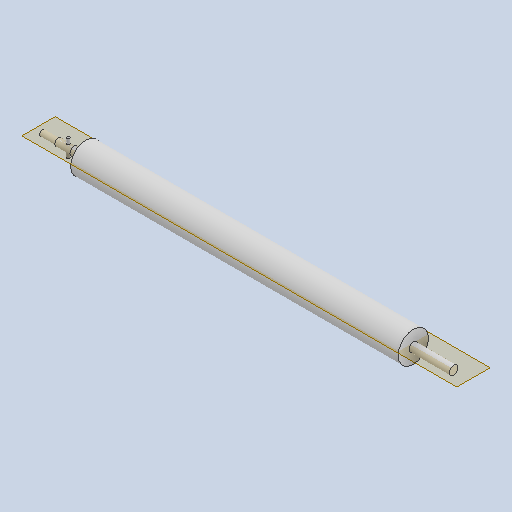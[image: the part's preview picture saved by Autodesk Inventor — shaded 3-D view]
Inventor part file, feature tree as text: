
AUTODESK INVENTOR PART (.ipt)
format: ipt  version: 2023 (Build 270158000, 158)  size: 115,712 bytes
history: native  units: in
note: dims shown in document units (in); Inventor stores cm internally (conversion verified against a paired STEP export)
features: extrude x6, sketch x6, plane x1
ambient origin geometry x8: Origin, YZ Plane, XZ Plane, XY Plane, X Axis, Y Axis, Z Axis, Center Point
bodies: Solid1 (feature_tree)
feature tree (13):
  extrude  "Extrusion1"  Depth=8.937in TaperAngle=0.0deg
  sketch  "Sketch2"  dims[d3=0.2362in d4=0.2362in]
  extrude  "Extrusion2"  Depth=0.2362in
  extrude  "Extrusion3"  Depth=0.315in TaperAngle=0.0deg
  extrude  "Extrusion4"  Depth=0.4331in TaperAngle=0.0deg
  plane  "Work Plane1"
  extrude  "Extrusion5"  Depth=0.0787in
  extrude  "Extrusion6"  Depth=0.1575in
  sketch  "Sketch1"  dims[d0=0.8268in d1=8.937in d2=0.0in]
  sketch  "Sketch3"  dims[d5=0.315in d6=0.0in d7=1.1024in d8=0.0in]
  sketch  "Sketch4"  dims[d9=0.1969in d10=0.4331in d11=0.0in]
  sketch  "Sketch5"  dims[d12=0.0787in d13=0.1575in]
  sketch  "Sketch6"  dims[d14=0.1378in d15=0.0in d16=0.1575in d17=0.4331in d18=0.0in d19=0.3346in d20=0.0in]
